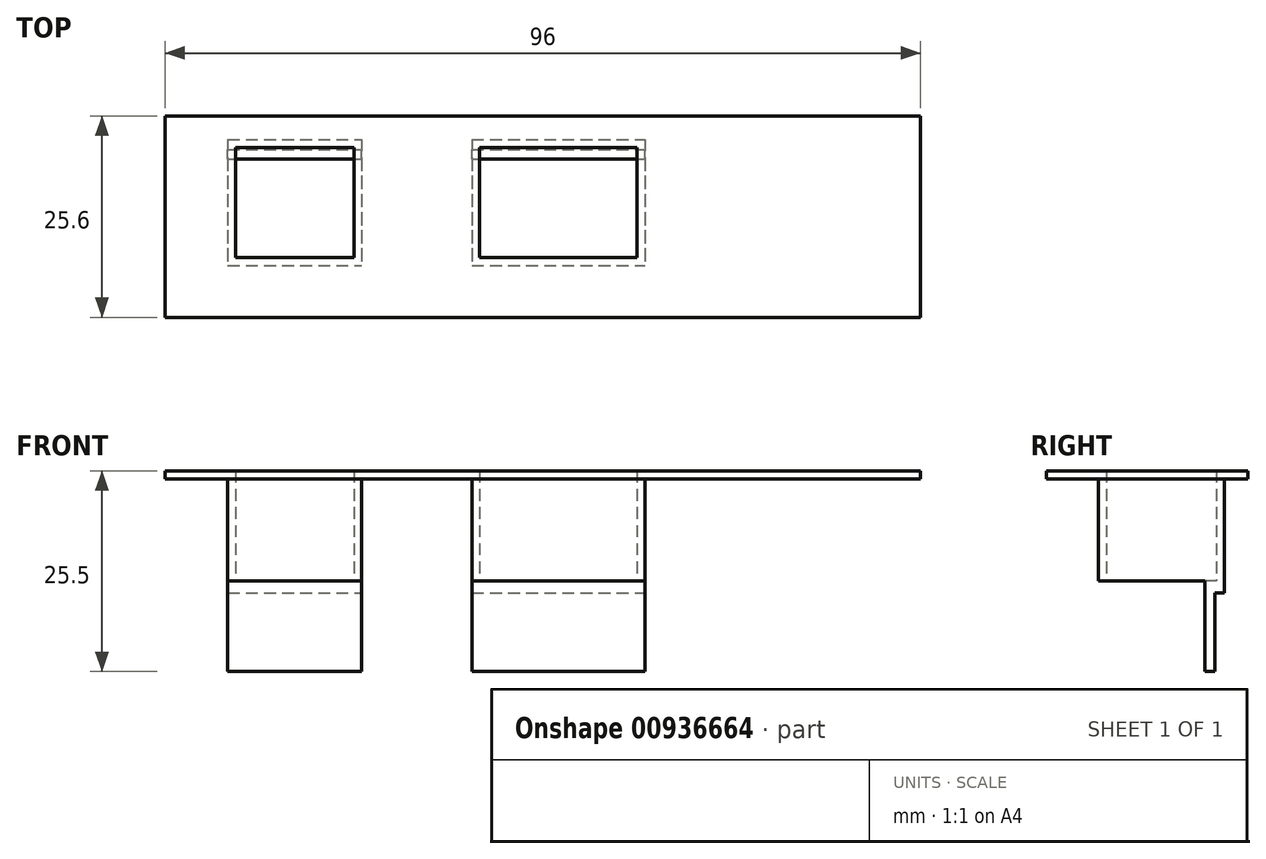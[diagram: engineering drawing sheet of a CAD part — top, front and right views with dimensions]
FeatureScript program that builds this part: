
annotation { "Feature Type Name" : "Feature", "Feature Type Description" : "" }
export const myFeature = defineFeature(function(context is Context, id is Id, definition is map)
    precondition{}
    {
        {
            var Q0;
            Q0=qCreatedBy(makeId("Top.planeOp"),FACE);
            var sketch = newSketch(context, id + "F0", { "sketchPlane" : qUnion([Q0])});
            skLineSegment(sketch, "E0.bottom", {"start": v(0, 0) * mm, "end": v(90, 0) * mm});
            skLineSegment(sketch, "E0.top", {"start": v(0, 19.6) * mm, "end": v(90, 19.6) * mm});
            skLineSegment(sketch, "E0.left", {"start": v(0, 0) * mm, "end": v(0, 19.6) * mm});
            skLineSegment(sketch, "E0.right", {"start": v(90, 0) * mm, "end": v(90, 19.6) * mm});
            skLineSegment(sketch, "E1.bottom", {"start": v(6, 18.6) * mm, "end": v(21, 18.6) * mm});
            skLineSegment(sketch, "E1.top", {"start": v(6, 4.6) * mm, "end": v(21, 4.6) * mm});
            skLineSegment(sketch, "E1.left", {"start": v(6, 18.6) * mm, "end": v(6, 4.6) * mm});
            skLineSegment(sketch, "E1.right", {"start": v(21, 18.6) * mm, "end": v(21, 4.6) * mm});
            skLineSegment(sketch, "E2.bottom", {"start": v(37, 18.6) * mm, "end": v(57, 18.6) * mm});
            skLineSegment(sketch, "E2.top", {"start": v(37, 4.6) * mm, "end": v(57, 4.6) * mm});
            skLineSegment(sketch, "E2.left", {"start": v(37, 18.6) * mm, "end": v(37, 4.6) * mm});
            skLineSegment(sketch, "E2.right", {"start": v(57, 18.6) * mm, "end": v(57, 4.6) * mm});
            skSolve(sketch);
        }
        {
            var Q0;
            Q0=makeQuery(id+"F0.imprint","IMPRINT",FACE,{"disambiguationData":[TD([[makeQuery(id+"F0.imprint","IMPRINT",EDGE,{"derivedFrom":sQuery(id+"F0.wireOp",EDGE,"E0.bottom")}),1.0]])]});
            extrude(context, id + "F1", {"entities" : qUnion([Q0]), "depth" : 1 * mm, "offsetDistance" : 25 * mm});
        }
        {
            var Q0;
            Q0=makeQuery(id+"F1.opExtrude","CAP_FACE",FACE,{"disambiguationData":[OSD([sQuery(id+"F0.wireOp",EDGE,"E0.bottom"),sQuery(id+"F0.wireOp",EDGE,"E0.top"),sQuery(id+"F0.wireOp",EDGE,"E0.left"),sQuery(id+"F0.wireOp",EDGE,"E0.right"),sQuery(id+"F0.wireOp",EDGE,"E1.bottom"),sQuery(id+"F0.wireOp",EDGE,"E1.top"),sQuery(id+"F0.wireOp",EDGE,"E1.left"),sQuery(id+"F0.wireOp",EDGE,"E1.right"),sQuery(id+"F0.wireOp",EDGE,"E2.bottom"),sQuery(id+"F0.wireOp",EDGE,"E2.top"),sQuery(id+"F0.wireOp",EDGE,"E2.left"),sQuery(id+"F0.wireOp",EDGE,"E2.right")])],"isStart":true});
            var sketch = newSketch(context, id + "F2", { "sketchPlane" : qUnion([Q0])});
            skLineSegment(sketch, "E3.0", {"start": v(6, -18.6) * mm, "end": v(6, -4.6) * mm});
            skLineSegment(sketch, "E3.1", {"start": v(6, -4.6) * mm, "end": v(21, -4.6) * mm});
            skLineSegment(sketch, "E3.2", {"start": v(21, -18.6) * mm, "end": v(21, -4.6) * mm});
            skLineSegment(sketch, "E3.3", {"start": v(6, -18.6) * mm, "end": v(21, -18.6) * mm});
            skLineSegment(sketch, "E3.4", {"start": v(37, -18.6) * mm, "end": v(37, -4.6) * mm});
            skLineSegment(sketch, "E3.5", {"start": v(37, -4.6) * mm, "end": v(57, -4.6) * mm});
            skLineSegment(sketch, "E3.6", {"start": v(57, -18.6) * mm, "end": v(57, -4.6) * mm});
            skLineSegment(sketch, "E3.7", {"start": v(37, -18.6) * mm, "end": v(57, -18.6) * mm});
            skLineSegment(sketch, "E4.0", {"start": v(5, -3.6) * mm, "end": v(22, -3.6) * mm});
            skLineSegment(sketch, "E4.1", {"start": v(5, -19.6) * mm, "end": v(5, -3.6) * mm});
            skLineSegment(sketch, "E4.2", {"start": v(5, -19.6) * mm, "end": v(22, -19.6) * mm});
            skLineSegment(sketch, "E4.3", {"start": v(22, -19.6) * mm, "end": v(22, -3.6) * mm});
            skLineSegment(sketch, "E5.0", {"start": v(36, -3.6) * mm, "end": v(58, -3.6) * mm});
            skLineSegment(sketch, "E5.1", {"start": v(36, -19.6) * mm, "end": v(36, -3.6) * mm});
            skLineSegment(sketch, "E5.2", {"start": v(36, -19.6) * mm, "end": v(58, -19.6) * mm});
            skLineSegment(sketch, "E5.3", {"start": v(58, -19.6) * mm, "end": v(58, -3.6) * mm});
            skSolve(sketch);
        }
        {
            var Q0;
            Q0 = qSketchRegion(id + "F2", true);
            extrude(context, id + "F3", {"entities" : qUnion([Q0]), "operationType" : NewBodyOperationType.ADD, "depth" : 13 * mm, "offsetDistance" : 25 * mm});
        }
        {
            var Q0;
            Q0=qCreatedBy(makeId("Top.planeOp"),FACE);
            var sketch = newSketch(context, id + "F4", { "sketchPlane" : qUnion([Q0])});
            skLineSegment(sketch, "E6.0", {"start": v(93, -3) * mm, "end": v(93, 22.6) * mm});
            skLineSegment(sketch, "E6.1", {"start": v(-3, -3) * mm, "end": v(93, -3) * mm});
            skLineSegment(sketch, "E6.2", {"start": v(-3, -3) * mm, "end": v(-3, 22.6) * mm});
            skLineSegment(sketch, "E6.3", {"start": v(-3, 22.6) * mm, "end": v(93, 22.6) * mm});
            skLineSegment(sketch, "E7.0", {"start": v(6, 4.6) * mm, "end": v(21, 4.6) * mm});
            skLineSegment(sketch, "E7.1", {"start": v(6, 18.6) * mm, "end": v(6, 4.6) * mm});
            skLineSegment(sketch, "E7.2", {"start": v(6, 18.6) * mm, "end": v(21, 18.6) * mm});
            skLineSegment(sketch, "E7.3", {"start": v(21, 18.6) * mm, "end": v(21, 4.6) * mm});
            skLineSegment(sketch, "E7.4", {"start": v(37, 18.6) * mm, "end": v(37, 4.6) * mm});
            skLineSegment(sketch, "E7.5", {"start": v(37, 4.6) * mm, "end": v(57, 4.6) * mm});
            skLineSegment(sketch, "E7.6", {"start": v(57, 18.6) * mm, "end": v(57, 4.6) * mm});
            skLineSegment(sketch, "E7.7", {"start": v(37, 18.6) * mm, "end": v(57, 18.6) * mm});
            skPoint(sketch, "E7.8", {"position": v(47, 4.6) * mm});
            skSolve(sketch);
        }
        {
            var Q0;
            Q0=makeQuery(id+"F4.imprint","IMPRINT",FACE,{"disambiguationData":[TD([[makeQuery(id+"F4.imprint","IMPRINT",EDGE,{"derivedFrom":sQuery(id+"F4.wireOp",EDGE,"E6.0")}),1.0]])]});
            var Q1;
            Q1=makeQuery(id+"F1.opExtrude","CAP_FACE",FACE,{"disambiguationData":[OSD([sQuery(id+"F0.wireOp",EDGE,"E0.bottom"),sQuery(id+"F0.wireOp",EDGE,"E0.top"),sQuery(id+"F0.wireOp",EDGE,"E0.left"),sQuery(id+"F0.wireOp",EDGE,"E0.right"),sQuery(id+"F0.wireOp",EDGE,"E1.bottom"),sQuery(id+"F0.wireOp",EDGE,"E1.top"),sQuery(id+"F0.wireOp",EDGE,"E1.left"),sQuery(id+"F0.wireOp",EDGE,"E1.right"),sQuery(id+"F0.wireOp",EDGE,"E2.bottom"),sQuery(id+"F0.wireOp",EDGE,"E2.top"),sQuery(id+"F0.wireOp",EDGE,"E2.left"),sQuery(id+"F0.wireOp",EDGE,"E2.right")])],"isStart":false});
            extrude(context, id + "F5", {"entities" : qUnion([Q0]), "operationType" : NewBodyOperationType.ADD, "endBound" : BoundingType.UP_TO_SURFACE, "depth" : 25 * mm, "endBoundEntityFace" : qUnion([Q1]), "offsetDistance" : 25 * mm});
        }
        {
            var Q0;
            Q0=makeQuery(id+"F3.opExtrude","CAP_FACE",FACE,{"disambiguationData":[OSD([sQuery(id+"F2.wireOp",EDGE,"E3.0"),sQuery(id+"F2.wireOp",EDGE,"E3.1"),sQuery(id+"F2.wireOp",EDGE,"E3.2"),sQuery(id+"F2.wireOp",EDGE,"E3.3"),sQuery(id+"F2.wireOp",EDGE,"E4.0"),sQuery(id+"F2.wireOp",EDGE,"E4.1"),sQuery(id+"F2.wireOp",EDGE,"E4.2"),sQuery(id+"F2.wireOp",EDGE,"E4.3")])],"isStart":false});
            var sketch = newSketch(context, id + "F6", { "sketchPlane" : qUnion([Q0])});
            skLineSegment(sketch, "E8.bottom", {"start": v(5, -19.6) * mm, "end": v(22, -19.6) * mm});
            skLineSegment(sketch, "E8.top", {"start": v(5, -17.1) * mm, "end": v(22, -17.1) * mm});
            skLineSegment(sketch, "E8.left", {"start": v(5, -19.6) * mm, "end": v(5, -17.1) * mm});
            skLineSegment(sketch, "E8.right", {"start": v(22, -19.6) * mm, "end": v(22, -17.1) * mm});
            skSolve(sketch);
        }
        {
            var Q0;
            Q0=makeQuery(id+"F3.opExtrude","CAP_FACE",FACE,{"disambiguationData":[OSD([sQuery(id+"F2.wireOp",EDGE,"E3.4"),sQuery(id+"F2.wireOp",EDGE,"E3.5"),sQuery(id+"F2.wireOp",EDGE,"E3.6"),sQuery(id+"F2.wireOp",EDGE,"E3.7"),sQuery(id+"F2.wireOp",EDGE,"E5.0"),sQuery(id+"F2.wireOp",EDGE,"E5.1"),sQuery(id+"F2.wireOp",EDGE,"E5.2"),sQuery(id+"F2.wireOp",EDGE,"E5.3")])],"isStart":false});
            var sketch = newSketch(context, id + "F7", { "sketchPlane" : qUnion([Q0])});
            skLineSegment(sketch, "E9.bottom", {"start": v(36, -19.6) * mm, "end": v(58, -19.6) * mm});
            skLineSegment(sketch, "E9.top", {"start": v(36, -17.1) * mm, "end": v(58, -17.1) * mm});
            skLineSegment(sketch, "E9.left", {"start": v(36, -19.6) * mm, "end": v(36, -17.1) * mm});
            skLineSegment(sketch, "E9.right", {"start": v(58, -19.6) * mm, "end": v(58, -17.1) * mm});
            skSolve(sketch);
        }
        {
            var Q0;
            Q0 = qSketchRegion(id + "F6", true);
            var Q1;
            Q1 = qSketchRegion(id + "F7", true);
            extrude(context, id + "F8", {"entities" : qUnion([Q0, Q1]), "operationType" : NewBodyOperationType.ADD, "depth" : 1.5 * mm, "offsetDistance" : 25 * mm});
        }
        {
            var Q0;
            Q0=makeQuery(id+"F8.opExtrude","CAP_VERTEX",VERTEX,{"disambiguationData":[OSD([sQuery(id+"F2.wireOp",EDGE,"E4.1"),sQuery(id+"F6.wireOp",EDGE,"E8.top"),sQuery(id+"F6.wireOp",EDGE,"E8.left")])],"isStart":false});
            var Q1;
            Q1=makeQuery(id+"F8.opExtrude","CAP_VERTEX",VERTEX,{"disambiguationData":[OSD([sQuery(id+"F6.wireOp",EDGE,"E8.bottom"),sQuery(id+"F6.wireOp",EDGE,"E8.right")])],"isStart":false});
            var Q2;
            Q2=makeQuery(id+"F8.opExtrude","CAP_VERTEX",VERTEX,{"disambiguationData":[OSD([sQuery(id+"F2.wireOp",EDGE,"E5.3"),sQuery(id+"F7.wireOp",EDGE,"E9.top"),sQuery(id+"F7.wireOp",EDGE,"E9.right")])],"isStart":false});
            cPlane(context, id + "F9", {"entities" : qUnion([Q0, Q1, Q2]), "cplaneType" : CPlaneType.THREE_POINT, "offset" : 25 * mm, "width" : 150 * mm, "height" : 150 * mm});
        }
        {
            var Q0;
            Q0=qCreatedBy(id+"F9.planeOp",FACE);
            var sketch = newSketch(context, id + "F10", { "sketchPlane" : qUnion([Q0])});
            skPoint(sketch, "E10.4", {"position": v(36, 18.35) * mm});
            skLineSegment(sketch, "E11.bottom", {"start": v(5, 17.1) * mm, "end": v(22, 17.1) * mm});
            skLineSegment(sketch, "E11.top", {"start": v(5, 18.35) * mm, "end": v(22, 18.35) * mm});
            skLineSegment(sketch, "E11.left", {"start": v(5, 17.1) * mm, "end": v(5, 18.35) * mm});
            skLineSegment(sketch, "E11.right", {"start": v(22, 17.1) * mm, "end": v(22, 18.35) * mm});
            skLineSegment(sketch, "E12.bottom", {"start": v(36, 17.1) * mm, "end": v(58, 17.1) * mm});
            skLineSegment(sketch, "E12.top", {"start": v(36, 18.35) * mm, "end": v(58, 18.35) * mm});
            skLineSegment(sketch, "E12.left", {"start": v(36, 17.1) * mm, "end": v(36, 18.35) * mm});
            skLineSegment(sketch, "E12.right", {"start": v(58, 17.1) * mm, "end": v(58, 18.35) * mm});
            skSolve(sketch);
        }
        {
            var Q0;
            Q0 = qSketchRegion(id + "F10", true);
            extrude(context, id + "F11", {"entities" : qUnion([Q0]), "operationType" : NewBodyOperationType.ADD, "oppositeDirection" : true, "depth" : 10 * mm, "offsetDistance" : 25 * mm});
        }
    });
